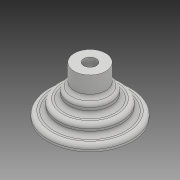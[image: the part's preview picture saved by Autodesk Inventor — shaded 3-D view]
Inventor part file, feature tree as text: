
AUTODESK INVENTOR PART (.ipt)
format: ipt  version: 2018 (Build 220112000, 112)  size: 177,152 bytes
history: native  units: mm
features: extrude x5, sketch x5, other x1, fillet x1
ambient origin geometry x8: Origin, YZ Plane, XZ Plane, XY Plane, X Axis, Y Axis, Z Axis, Center Point
bodies: Body1 (feature_tree)
feature tree (12):
  other  "Sólido1"
  extrude  "Extrusión1"  Depth=3.0mm TaperAngle=0.0deg
  extrude  "Extrusión2"  Depth=5.0mm TaperAngle=0.0deg
  extrude  "Extrusión3"  Depth=15.0mm
  extrude  "Extrusión4"  Depth=20.0mm
  extrude  "Extrusión5"  Depth=20.0mm TaperAngle=0.0deg
  fillet  "Empalme1"  Radius=2.0mm
  sketch  "Boceto1"  dims[d0=40.0mm d1=3.0mm d2=0.0mm]
  sketch  "Boceto2"  dims[d3=30.0mm d4=5.0mm d5=0.0mm]
  sketch  "Boceto3"  dims[d6=6.0mm d7=15.0mm]
  sketch  "Boceto4"  dims[d8=15.0mm d9=0.0mm d10=20.0mm]
  sketch  "Boceto5"  dims[d11=5.0mm d12=0.0mm d13=20.0mm d14=0.0mm d15=2.0mm]
